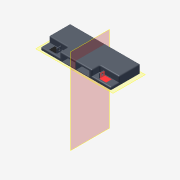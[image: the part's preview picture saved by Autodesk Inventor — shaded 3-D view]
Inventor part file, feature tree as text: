
AUTODESK INVENTOR PART (.ipt)
format: ipt  version: 2014 (Build 180170000, 170)  size: 363,008 bytes
history: native  units: mm (DEFAULTED — no unit token found)
features: sketch x10, extrude x9, fillet x5, plane x5, mirror x3, split x3, hole x1
ambient origin geometry x8: Origin, YZ Plane, XZ Plane, XY Plane, X Axis, Y Axis, Z Axis, Center Point
bodies: Solid1 (feature_tree)
feature tree (36):
  extrude  "Extrusion1"  Depth=74.422mm
  extrude  "Extrusion2"  Depth=139.7mm TaperAngle=0.0deg
  extrude  "Extrusion3"  Depth=21.336mm
  fillet  "Fillet1"  Radius=14.224mm
  fillet  "Fillet3"  Radius=2.54mm
  fillet  "Fillet4"  Radius=2.54mm
  extrude  "Extrusion4"  Depth=0.254mm TaperAngle=0.0deg
  extrude  "Extrusion5"  Depth=12.7mm TaperAngle=0.0deg
  extrude  "Extrusion6"  Depth=12.7mm TaperAngle=0.0deg
  plane  "Work Plane1"
  mirror  "Mirror1"
  mirror  "Mirror2"
  extrude  "Extrusion7"  Depth=20.32mm
  extrude  "Extrusion8"  Depth=19.558mm TaperAngle=0.0deg
  plane  "Work Plane2"
  fillet  "Fillet5"  Radius=33.02mm
  plane  "Work Plane3"
  extrude  "Extrusion9"  Depth=19.05mm TaperAngle=0.0deg
  hole  "Hole1"  [1 undecoded]
  fillet  "Fillet6"  Radius=56.261mm
  mirror  "Mirror3"
  plane  "Work Plane4"
  split  "Split2"
  plane  "Work Plane6"
  split  "Split3"
  split  "Split4"
  sketch  "Sketch1"  dims[d0=179.578mm d1=74.422mm]
  sketch  "Sketch2"  dims[d2=139.7mm d3=0.0mm d4=21.082mm d5=0.0mm]
  sketch  "Sketch3"  dims[d6=49.276mm d7=21.336mm d8=14.224mm d9=0.0mm d10=2.54mm d12=2.54mm]
  sketch  "Sketch4"  dims[d13=2.54mm d14=0.254mm d15=0.0mm]
  sketch  "Sketch5"  dims[d16=1.524mm d17=12.7mm d18=0.0mm]
  sketch  "Sketch6"  dims[d19=5.08mm d20=12.7mm d21=0.0mm]
  sketch  "Sketch7"  dims[d22=20.32mm d23=20.32mm]
  sketch  "Sketch8"  dims[d24=63.5mm d25=19.558mm d26=0.0mm d27=33.02mm]
  sketch  "Sketch9"  dims[d28=3.048mm d29=19.05mm d30=0.0mm]
  sketch  "Sketch10"  dims[d31=181.102mm d32=-127.0mm d34=1.27mm d35=56.261mm d36=11.9888mm d37=11.5062mm d38=2.0066mm d39=0.0mm d40=5.4864mm d41=5.4864mm d42=19.05mm d43=9.525mm d44=6.35mm d45=14.3117mm d46=25.4mm d47=20.594885mm d48=1.27mm d49=14.986mm d50=90.0deg d51=0.0mm]
note: 1 required parameter value undecoded (feature->parameter linkage not recoverable at this tier; creation-order binding heuristic only, values carry confidence <= 0.55)
